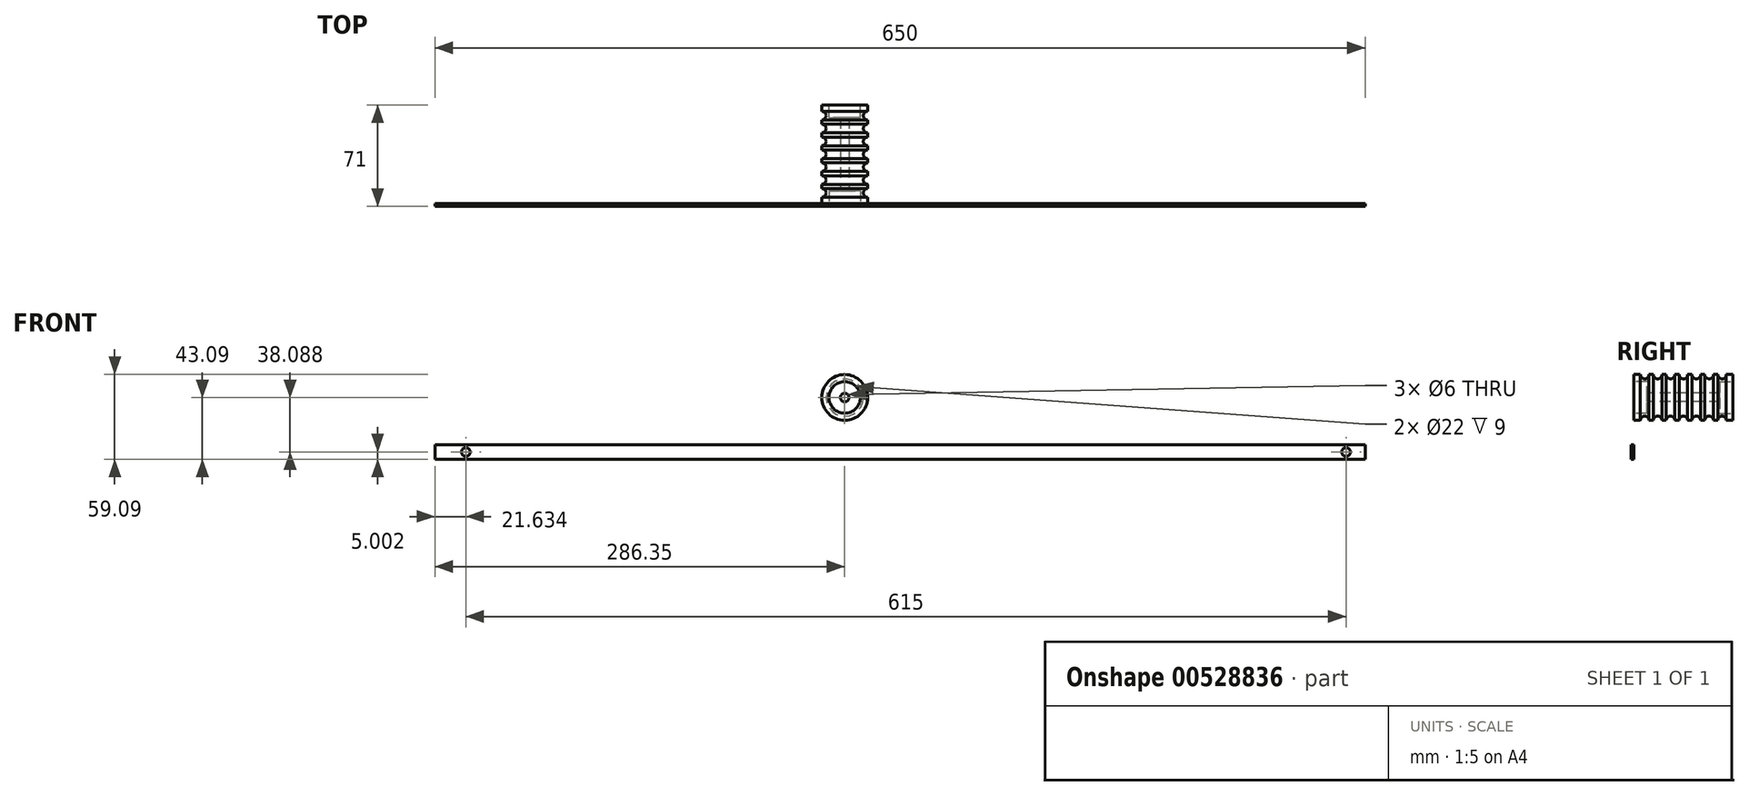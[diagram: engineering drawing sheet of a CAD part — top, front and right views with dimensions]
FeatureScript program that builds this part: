
annotation { "Feature Type Name" : "Feature", "Feature Type Description" : "" }
export const myFeature = defineFeature(function(context is Context, id is Id, definition is map)
    precondition{}
    {
        {
            var Q0;
            Q0=qCreatedBy(makeId("Front.planeOp"),FACE);
            var sketch = newSketch(context, id + "F0", { "sketchPlane" : qUnion([Q0])});
            skCircle(sketch, "E0", {"center": v(0, 0) * mm, "radius": 16 * mm});
            skSolve(sketch);
        }
        {
            var Q0;
            Q0 = qSketchRegion(id + "F0", true);
            extrude(context, id + "F1", {"entities" : qUnion([Q0]), "endBound" : BoundingType.SYMMETRIC, "depth" : 69 * mm, "offsetDistance" : 25 * mm});
        }
        {
            var Q0;
            Q0=qCreatedBy(makeId("Right.planeOp"),FACE);
            var sketch = newSketch(context, id + "F2", { "sketchPlane" : qUnion([Q0])});
            skCircle(sketch, "E1", {"center": v(0, 16) * mm, "radius": 3 * mm});
            skCircle(sketch, "E2.1.0.0", {"center": v(9, 16) * mm, "radius": 3 * mm});
            skCircle(sketch, "E2.2.0.0", {"center": v(18, 16) * mm, "radius": 3 * mm});
            skCircle(sketch, "E2.3.0.0", {"center": v(27, 16) * mm, "radius": 3 * mm});
            skLineSegment(sketch, "E2.direction1", {"start": v(0, 16) * mm, "end": v(9, 16) * mm, "construction": true});
            skCircle(sketch, "E3.1.0.0", {"center": v(-9, 16) * mm, "radius": 3 * mm});
            skCircle(sketch, "E3.2.0.0", {"center": v(-18, 16) * mm, "radius": 3 * mm});
            skCircle(sketch, "E3.3.0.0", {"center": v(-27, 16) * mm, "radius": 3 * mm});
            skLineSegment(sketch, "E3.direction1", {"start": v(0, 16) * mm, "end": v(-9, 16) * mm, "construction": true});
            skSolve(sketch);
        }
        {
            var Q0;
            Q0=makeQuery(id+"F2.imprint","IMPRINT",FACE,{"disambiguationData":[TD([[makeQuery(id+"F2.imprint","IMPRINT",EDGE,{"derivedFrom":sQuery(id+"F2.wireOp",EDGE,"E3.3.0.0")}),1.0]])]});
            var Q1;
            Q1=makeQuery(id+"F2.imprint","IMPRINT",FACE,{"disambiguationData":[TD([[makeQuery(id+"F2.imprint","IMPRINT",EDGE,{"derivedFrom":sQuery(id+"F2.wireOp",EDGE,"E3.2.0.0")}),1.0]])]});
            var Q2;
            Q2=makeQuery(id+"F2.imprint","IMPRINT",FACE,{"disambiguationData":[TD([[makeQuery(id+"F2.imprint","IMPRINT",EDGE,{"derivedFrom":sQuery(id+"F2.wireOp",EDGE,"E3.1.0.0")}),1.0]])]});
            var Q3;
            Q3=makeQuery(id+"F2.imprint","IMPRINT",FACE,{"disambiguationData":[TD([[makeQuery(id+"F2.imprint","IMPRINT",EDGE,{"derivedFrom":sQuery(id+"F2.wireOp",EDGE,"E1")}),1.0]])]});
            var Q4;
            Q4=makeQuery(id+"F2.imprint","IMPRINT",FACE,{"disambiguationData":[TD([[makeQuery(id+"F2.imprint","IMPRINT",EDGE,{"derivedFrom":sQuery(id+"F2.wireOp",EDGE,"E2.1.0.0")}),1.0]])]});
            var Q5;
            Q5=makeQuery(id+"F2.imprint","IMPRINT",FACE,{"disambiguationData":[TD([[makeQuery(id+"F2.imprint","IMPRINT",EDGE,{"derivedFrom":sQuery(id+"F2.wireOp",EDGE,"E2.2.0.0")}),1.0]])]});
            var Q6;
            Q6=makeQuery(id+"F2.imprint","IMPRINT",FACE,{"disambiguationData":[TD([[makeQuery(id+"F2.imprint","IMPRINT",EDGE,{"derivedFrom":sQuery(id+"F2.wireOp",EDGE,"E2.3.0.0")}),1.0]])]});
            var Q7;
            Q7=makeQuery(id+"F1.opExtrude","CAP_EDGE",EDGE,{"disambiguationData":[OSD([sQuery(id+"F0.wireOp",EDGE,"E0")])],"isStart":false});
            revolve(context, id + "F3", {"operationType" : NewBodyOperationType.REMOVE, "entities" : qUnion([Q0, Q1, Q2, Q3, Q4, Q5, Q6]), "axis" : qUnion([Q7]), "revolveType" : RevolveType.FULL, "oppositeDirection" : true});
        }
        {
            var Q0;
            Q0=makeQuery(id+"F1.opExtrude","CAP_FACE",FACE,{"disambiguationData":[OSD([sQuery(id+"F0.wireOp",EDGE,"E0")])],"isStart":false});
            var sketch = newSketch(context, id + "F4", { "sketchPlane" : qUnion([Q0])});
            skCircle(sketch, "E4", {"center": v(0, 0) * mm, "radius": 3 * mm});
            skSolve(sketch);
        }
        {
            var Q0;
            Q0=makeQuery(id+"F4.imprint","IMPRINT",FACE,{"disambiguationData":[TD([[makeQuery(id+"F4.imprint","IMPRINT",EDGE,{"derivedFrom":sQuery(id+"F4.wireOp",EDGE,"E4")}),1.0]])]});
            extrude(context, id + "F5", {"entities" : qUnion([Q0]), "operationType" : NewBodyOperationType.REMOVE, "endBound" : BoundingType.THROUGH_ALL, "oppositeDirection" : true, "depth" : 25 * mm, "offsetDistance" : 25 * mm});
        }
        {
            var Q0;
            Q0=makeQuery(id+"F1.opExtrude","CAP_FACE",FACE,{"disambiguationData":[OSD([sQuery(id+"F0.wireOp",EDGE,"E0")])],"isStart":false});
            var sketch = newSketch(context, id + "F6", { "sketchPlane" : qUnion([Q0])});
            skCircle(sketch, "E5", {"center": v(0, 0) * mm, "radius": 11 * mm});
            skSolve(sketch);
        }
        {
            var Q0;
            Q0=makeQuery(id+"F6.imprint","IMPRINT",FACE,{"disambiguationData":[TD([[makeQuery(id+"F6.imprint","IMPRINT",EDGE,{"derivedFrom":sQuery(id+"F6.wireOp",EDGE,"E5")}),1.0]])]});
            extrude(context, id + "F7", {"entities" : qUnion([Q0]), "operationType" : NewBodyOperationType.REMOVE, "oppositeDirection" : true, "depth" : 9 * mm, "offsetDistance" : 25 * mm});
        }
        {
            var Q0;
            Q0=makeQuery(id+"F1.opExtrude","CAP_FACE",FACE,{"disambiguationData":[OSD([sQuery(id+"F0.wireOp",EDGE,"E0")])],"isStart":true});
            var sketch = newSketch(context, id + "F8", { "sketchPlane" : qUnion([Q0])});
            skCircle(sketch, "E6", {"center": v(0, 0) * mm, "radius": 11 * mm});
            skSolve(sketch);
        }
        {
            var Q0;
            Q0=makeQuery(id+"F8.imprint","IMPRINT",FACE,{"disambiguationData":[TD([[makeQuery(id+"F8.imprint","IMPRINT",EDGE,{"derivedFrom":sQuery(id+"F8.wireOp",EDGE,"E6")}),1.0]])]});
            extrude(context, id + "F9", {"entities" : qUnion([Q0]), "operationType" : NewBodyOperationType.REMOVE, "oppositeDirection" : true, "depth" : 9 * mm, "offsetDistance" : 25 * mm});
        }
        {
            var Q0;
            Q0=makeQuery(id+"F1.opExtrude","CAP_FACE",FACE,{"disambiguationData":[OSD([sQuery(id+"F0.wireOp",EDGE,"E0")])],"isStart":false});
            var sketch = newSketch(context, id + "F10", { "sketchPlane" : qUnion([Q0])});
            skLineSegment(sketch, "E7.bottom", {"start": v(363.65, -43.09) * mm, "end": v(-286.35, -43.09) * mm});
            skLineSegment(sketch, "E7.top", {"start": v(363.65, -33.09) * mm, "end": v(-286.35, -33.09) * mm});
            skLineSegment(sketch, "E7.left", {"start": v(363.65, -43.09) * mm, "end": v(363.65, -33.09) * mm});
            skLineSegment(sketch, "E7.right", {"start": v(-286.35, -43.09) * mm, "end": v(-286.35, -33.09) * mm});
            skSolve(sketch);
        }
        {
            var Q0;
            Q0=makeQuery(id+"F10.imprint","IMPRINT",FACE,{"disambiguationData":[TD([[makeQuery(id+"F10.imprint","IMPRINT",EDGE,{"derivedFrom":sQuery(id+"F10.wireOp",EDGE,"E7.bottom")}),-1.0]])]});
            extrude(context, id + "F11", {"entities" : qUnion([Q0]), "depth" : 2 * mm, "offsetDistance" : 25 * mm});
        }
        {
            var Q0;
            Q0=makeQuery(id+"F11.opExtrude","CAP_FACE",FACE,{"disambiguationData":[OSD([sQuery(id+"F10.wireOp",EDGE,"E7.bottom"),sQuery(id+"F10.wireOp",EDGE,"E7.top"),sQuery(id+"F10.wireOp",EDGE,"E7.left"),sQuery(id+"F10.wireOp",EDGE,"E7.right")])],"isStart":false});
            var sketch = newSketch(context, id + "F12", { "sketchPlane" : qUnion([Q0])});
            skLineSegment(sketch, "E8", {"start": v(363.65, -38.09) * mm, "end": v(323.71, -38.09) * mm});
            skPoint(sketch, "E8.endSnap0", {"position": v(363.65, -38.09) * mm});
            skCircle(sketch, "E9", {"center": v(350.28, -38.09) * mm, "radius": 3 * mm});
            skCircle(sketch, "E10", {"center": v(-264.72, -38.09) * mm, "radius": 3 * mm});
            skPoint(sketch, "E10.centerSnap0", {"position": v(-286.35, -38.09) * mm});
            skSolve(sketch);
        }
        {
            var Q0;
            {var subQ0=sQuery(id+"F12.wireOp",EDGE,"E9");var subQ1=sQuery(id+"F12.wireOp",EDGE,"E8");var subQ2=makeQuery(id+"F12.imprint","INTERSECT",VERTEX,{"disambiguationData":[OD(0.0)],"derivedFrom":[subQ1,subQ0]});Q0=makeQuery(id+"F12.imprint","IMPRINT",FACE,{"disambiguationData":[TD([[makeQuery(id+"F12.imprint","IMPRINT",EDGE,{"disambiguationData":[TD([[subQ2,1.0]])],"derivedFrom":subQ1}),1.0]])]});}
            var Q1;
            {var subQ0=sQuery(id+"F12.wireOp",EDGE,"E9");var subQ1=sQuery(id+"F12.wireOp",EDGE,"E8");var subQ2=makeQuery(id+"F12.imprint","INTERSECT",VERTEX,{"disambiguationData":[OD(0.0)],"derivedFrom":[subQ1,subQ0]});Q1=makeQuery(id+"F12.imprint","IMPRINT",FACE,{"disambiguationData":[TD([[makeQuery(id+"F12.imprint","IMPRINT",EDGE,{"disambiguationData":[TD([[subQ2,1.0]])],"derivedFrom":subQ1}),-1.0]])]});}
            var Q2;
            Q2=makeQuery(id+"F12.imprint","IMPRINT",FACE,{"disambiguationData":[TD([[makeQuery(id+"F12.imprint","IMPRINT",EDGE,{"derivedFrom":sQuery(id+"F12.wireOp",EDGE,"E10")}),1.0]])]});
            extrude(context, id + "F13", {"entities" : qUnion([Q0, Q1, Q2]), "operationType" : NewBodyOperationType.REMOVE, "oppositeDirection" : true, "depth" : 25 * mm, "offsetDistance" : 25 * mm});
        }
    });
